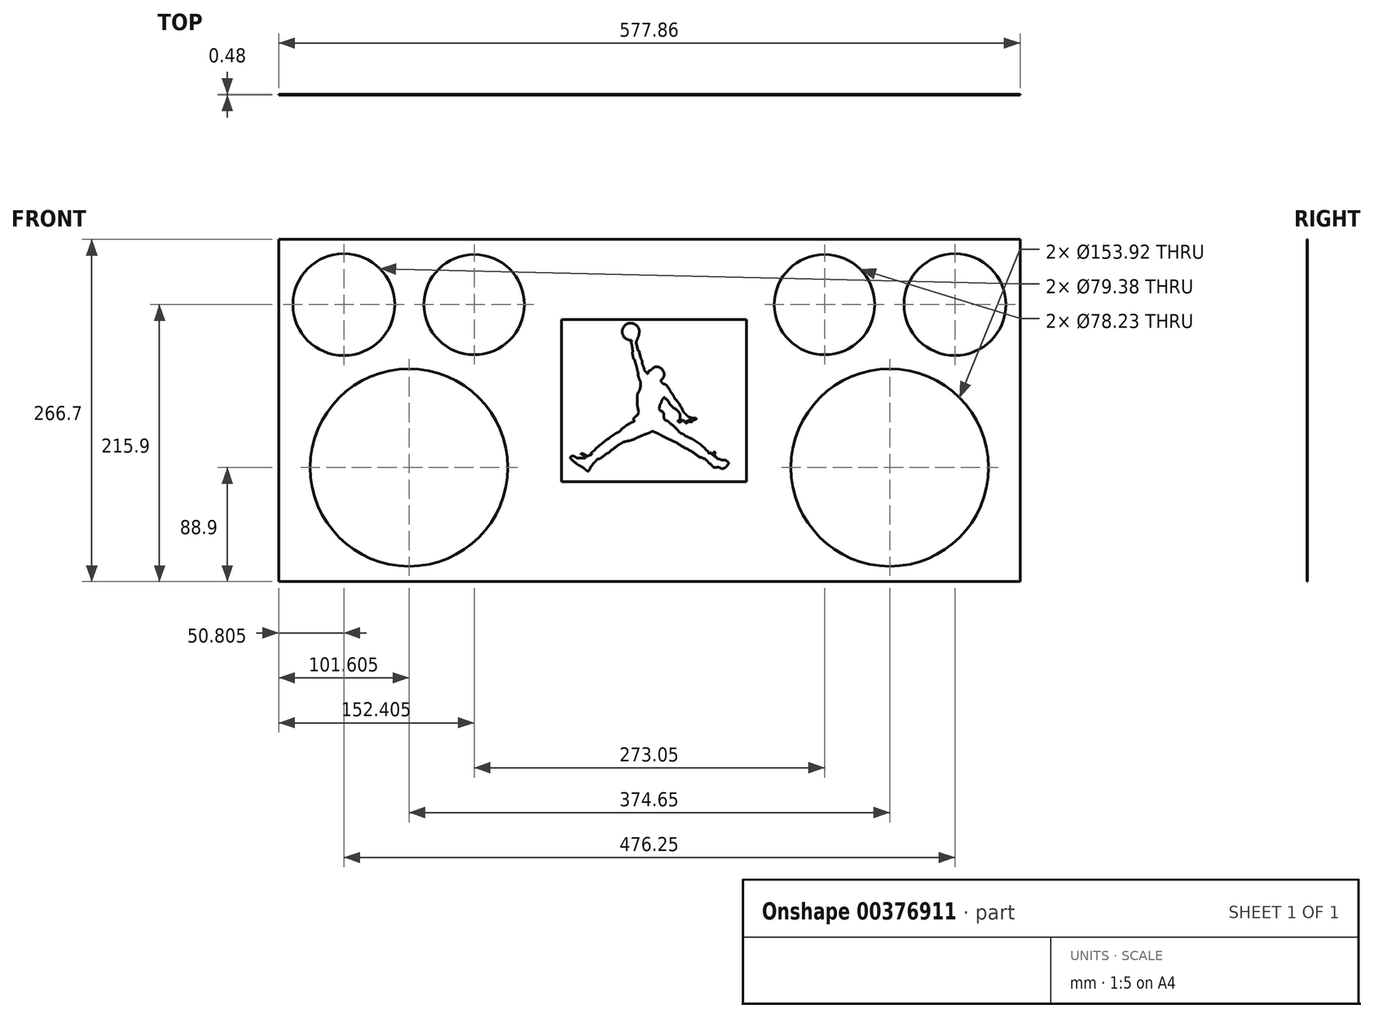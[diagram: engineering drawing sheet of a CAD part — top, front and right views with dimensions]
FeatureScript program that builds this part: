
annotation { "Feature Type Name" : "Feature", "Feature Type Description" : "" }
export const myFeature = defineFeature(function(context is Context, id is Id, definition is map)
    precondition{}
    {
        {
            var Q0;
            Q0=qCreatedBy(makeId("Front.planeOp"),FACE);
            var sketch = newSketch(context, id + "F0", { "sketchPlane" : qUnion([Q0])});
            skLineSegment(sketch, "E0.bottom", {"start": v(288.93, -133.35) * mm, "end": v(-288.92, -133.35) * mm});
            skLineSegment(sketch, "E0.top", {"start": v(288.92, 133.35) * mm, "end": v(-288.93, 133.35) * mm});
            skLineSegment(sketch, "E0.left", {"start": v(288.93, -133.35) * mm, "end": v(288.93, 133.35) * mm});
            skLineSegment(sketch, "E0.right", {"start": v(-288.92, -133.35) * mm, "end": v(-288.93, 133.35) * mm});
            skPoint(sketch, "E0.middle", {"position": v(0, 0) * mm});
            skLineSegment(sketch, "E1.bottom", {"start": v(288.92, 133.35) * mm, "end": v(85.72, 133.35) * mm, "construction": true});
            skLineSegment(sketch, "E1.top", {"start": v(288.93, -133.35) * mm, "end": v(85.73, -133.35) * mm, "construction": true});
            skLineSegment(sketch, "E1.left", {"start": v(288.93, 133.35) * mm, "end": v(288.93, -133.35) * mm, "construction": true});
            skLineSegment(sketch, "E1.right", {"start": v(85.72, 133.35) * mm, "end": v(85.73, -133.35) * mm, "construction": true});
            skLineSegment(sketch, "E2.bottom", {"start": v(-288.93, 133.35) * mm, "end": v(-85.73, 133.35) * mm, "construction": true});
            skLineSegment(sketch, "E2.top", {"start": v(-288.92, -133.35) * mm, "end": v(-85.72, -133.35) * mm, "construction": true});
            skLineSegment(sketch, "E2.left", {"start": v(-288.93, 133.35) * mm, "end": v(-288.92, -133.35) * mm, "construction": true});
            skLineSegment(sketch, "E2.right", {"start": v(-85.73, 133.35) * mm, "end": v(-85.72, -133.35) * mm, "construction": true});
            skLineSegment(sketch, "E3.bottom", {"start": v(288.92, 133.35) * mm, "end": v(187.32, 133.35) * mm, "construction": true});
            skLineSegment(sketch, "E3.top", {"start": v(288.93, -133.35) * mm, "end": v(187.33, -133.35) * mm, "construction": true});
            skLineSegment(sketch, "E3.left", {"start": v(288.92, 133.35) * mm, "end": v(288.93, -133.35) * mm, "construction": true});
            skLineSegment(sketch, "E3.right", {"start": v(187.32, 133.35) * mm, "end": v(187.33, -133.35) * mm, "construction": true});
            skLineSegment(sketch, "E4.bottom", {"start": v(-288.93, 133.35) * mm, "end": v(-187.33, 133.35) * mm, "construction": true});
            skLineSegment(sketch, "E4.top", {"start": v(-288.92, -133.35) * mm, "end": v(-187.33, -133.35) * mm, "construction": true});
            skLineSegment(sketch, "E4.left", {"start": v(-288.93, 133.35) * mm, "end": v(-288.93, -133.35) * mm, "construction": true});
            skLineSegment(sketch, "E4.right", {"start": v(-187.32, 133.35) * mm, "end": v(-187.32, -133.35) * mm, "construction": true});
            skLineSegment(sketch, "E5.bottom", {"start": v(-280.92, -133.35) * mm, "end": v(281.55, -133.35) * mm, "construction": true});
            skLineSegment(sketch, "E5.top", {"start": v(-280.92, -44.45) * mm, "end": v(281.55, -44.45) * mm, "construction": true});
            skLineSegment(sketch, "E5.left", {"start": v(-280.92, -133.35) * mm, "end": v(-280.92, -44.45) * mm, "construction": true});
            skLineSegment(sketch, "E5.right", {"start": v(281.55, -133.35) * mm, "end": v(281.55, -44.45) * mm, "construction": true});
            skCircle(sketch, "E6", {"center": v(-187.33, -44.45) * mm, "radius": 76.96 * mm});
            skCircle(sketch, "E7", {"center": v(187.33, -44.45) * mm, "radius": 76.96 * mm});
            skLineSegment(sketch, "E8.bottom", {"start": v(-279.46, 133.35) * mm, "end": v(276.06, 133.35) * mm, "construction": true});
            skLineSegment(sketch, "E8.top", {"start": v(-279.46, 82.55) * mm, "end": v(276.06, 82.55) * mm, "construction": true});
            skLineSegment(sketch, "E8.left", {"start": v(-279.46, 133.35) * mm, "end": v(-279.46, 82.55) * mm, "construction": true});
            skLineSegment(sketch, "E8.right", {"start": v(276.06, 133.35) * mm, "end": v(276.06, 82.55) * mm, "construction": true});
            skLineSegment(sketch, "E9.bottom", {"start": v(-288.93, 99.85) * mm, "end": v(-238.12, 99.85) * mm, "construction": true});
            skLineSegment(sketch, "E9.top", {"start": v(-288.93, -125.6) * mm, "end": v(-238.12, -125.6) * mm, "construction": true});
            skLineSegment(sketch, "E9.left", {"start": v(-288.93, 99.85) * mm, "end": v(-288.93, -125.6) * mm, "construction": true});
            skLineSegment(sketch, "E9.right", {"start": v(-238.13, 99.85) * mm, "end": v(-238.13, -125.6) * mm, "construction": true});
            skLineSegment(sketch, "E10.bottom", {"start": v(288.93, 112.58) * mm, "end": v(238.12, 112.58) * mm, "construction": true});
            skLineSegment(sketch, "E10.top", {"start": v(288.93, -125.6) * mm, "end": v(238.12, -125.6) * mm, "construction": true});
            skLineSegment(sketch, "E10.left", {"start": v(288.93, 112.58) * mm, "end": v(288.93, -125.6) * mm, "construction": true});
            skLineSegment(sketch, "E10.right", {"start": v(238.12, 112.58) * mm, "end": v(238.12, -125.6) * mm, "construction": true});
            skCircle(sketch, "E11", {"center": v(-238.12, 82.55) * mm, "radius": 39.69 * mm});
            skCircle(sketch, "E12", {"center": v(238.12, 82.55) * mm, "radius": 39.69 * mm});
            skLineSegment(sketch, "E13.bottom", {"start": v(-85.73, 133.35) * mm, "end": v(-136.53, 133.35) * mm, "construction": true});
            skLineSegment(sketch, "E13.top", {"start": v(-85.73, 57.15) * mm, "end": v(-136.53, 57.15) * mm, "construction": true});
            skLineSegment(sketch, "E13.left", {"start": v(-85.73, 133.35) * mm, "end": v(-85.73, 57.15) * mm, "construction": true});
            skLineSegment(sketch, "E13.right", {"start": v(-136.53, 133.35) * mm, "end": v(-136.53, 57.15) * mm, "construction": true});
            skCircle(sketch, "E14", {"center": v(-136.53, 82.55) * mm, "radius": 39.12 * mm});
            skLineSegment(sketch, "E15.bottom", {"start": v(85.72, 133.35) * mm, "end": v(136.52, 133.35) * mm, "construction": true});
            skLineSegment(sketch, "E15.top", {"start": v(85.72, 47.73) * mm, "end": v(136.52, 47.73) * mm, "construction": true});
            skLineSegment(sketch, "E15.left", {"start": v(85.72, 133.35) * mm, "end": v(85.72, 47.73) * mm, "construction": true});
            skLineSegment(sketch, "E15.right", {"start": v(136.52, 133.35) * mm, "end": v(136.52, 47.73) * mm, "construction": true});
            skCircle(sketch, "E16", {"center": v(136.52, 82.55) * mm, "radius": 39.12 * mm});
            skSolve(sketch);
        }
        {
            assignVariable(context, id + "F1", {"name" : "material", "anyValue" : 0.47});
        }
        {
            var Q0;
            Q0=makeQuery(id+"F0.imprint","IMPRINT",FACE,{"disambiguationData":[TD([[makeQuery(id+"F0.imprint","IMPRINT",EDGE,{"derivedFrom":sQuery(id+"F0.wireOp",EDGE,"E0.bottom")}),-1.0]])]});
            extrude(context, id + "F2", {"entities" : qUnion([Q0]), "depth" : (getVariable(context, 'material')) * mm});
        }
        {
            var Q0;
            Q0=makeQuery(id+"F2.opExtrude","CAP_FACE",FACE,{"disambiguationData":[OSD([sQuery(id+"F0.wireOp",EDGE,"E0.bottom"),sQuery(id+"F0.wireOp",EDGE,"E0.top"),sQuery(id+"F0.wireOp",EDGE,"E0.left"),sQuery(id+"F0.wireOp",EDGE,"E0.right"),sQuery(id+"F0.wireOp",EDGE,"E6"),sQuery(id+"F0.wireOp",EDGE,"E7"),sQuery(id+"F0.wireOp",EDGE,"E11"),sQuery(id+"F0.wireOp",EDGE,"E12"),sQuery(id+"F0.wireOp",EDGE,"E14"),sQuery(id+"F0.wireOp",EDGE,"E16")])],"isStart":false});
            var sketch = newSketch(context, id + "F3", { "sketchPlane" : qUnion([Q0])});
            skArc(sketch, "E17.MirrorCS", {"start": v(46.02, -33.08) * mm, "mid": v(46.45, -33.28) * mm, "end": v(46.78, -33.62) * mm});
            skArc(sketch, "E18.MirrorCS", {"start": v(29.12, -9.84) * mm, "mid": v(28.78, -9.84) * mm, "end": v(28.45, -9.72) * mm});
            skLineSegment(sketch, "E19.MirrorCS", {"start": v(27.65, -9.13) * mm, "end": v(26.45, -7.69) * mm});
            skArc(sketch, "E20.MirrorCS", {"start": v(25.86, -7.66) * mm, "mid": v(25.2, -8.36) * mm, "end": v(24.35, -8.84) * mm});
            skArc(sketch, "E21.MirrorCS", {"start": v(48.94, -34.48) * mm, "mid": v(48.74, -34.18) * mm, "end": v(48.6, -33.86) * mm});
            skArc(sketch, "E22.MirrorCS", {"start": v(22.6, -8.8) * mm, "mid": v(22.38, -8.4) * mm, "end": v(22.47, -7.94) * mm});
            skArc(sketch, "E23.MirrorCS", {"start": v(24.1, -6.5) * mm, "mid": v(24.14, -6.74) * mm, "end": v(24.08, -7) * mm});
            skArc(sketch, "E24.MirrorCS", {"start": v(29.13, -8.1) * mm, "mid": v(29.78, -8.23) * mm, "end": v(30.4, -8.49) * mm});
            skArc(sketch, "E25.MirrorCS", {"start": v(50.79, -35.79) * mm, "mid": v(50.51, -35.77) * mm, "end": v(50.54, -35.5) * mm});
            skArc(sketch, "E26.MirrorCS", {"start": v(28.96, -8.36) * mm, "mid": v(29.24, -8.75) * mm, "end": v(29.47, -9.17) * mm});
            skArc(sketch, "E27.MirrorCS", {"start": v(51.39, -35.73) * mm, "mid": v(51.83, -35.97) * mm, "end": v(52.13, -36.38) * mm});
            skArc(sketch, "E28.MirrorCS", {"start": v(46.02, -33.08) * mm, "mid": v(45.92, -32.9) * mm, "end": v(46.09, -32.78) * mm});
            skArc(sketch, "E29.MirrorCS", {"start": v(29.47, -9.17) * mm, "mid": v(29.47, -9.6) * mm, "end": v(29.12, -9.84) * mm});
            skArc(sketch, "E30.MirrorCS", {"start": v(28.9, -3.43) * mm, "mid": v(29.28, -3.81) * mm, "end": v(29.6, -4.23) * mm});
            skArc(sketch, "E31.MirrorCS", {"start": v(28.45, -9.72) * mm, "mid": v(28.03, -9.45) * mm, "end": v(27.65, -9.13) * mm});
            skArc(sketch, "E32.MirrorCS", {"start": v(48.03, -33.13) * mm, "mid": v(48.4, -33.43) * mm, "end": v(48.6, -33.86) * mm});
            skArc(sketch, "E33.MirrorCS", {"start": v(25.86, -7.66) * mm, "mid": v(26.16, -7.56) * mm, "end": v(26.45, -7.69) * mm});
            skArc(sketch, "E34.MirrorCS", {"start": v(24.35, -8.84) * mm, "mid": v(23.47, -9.05) * mm, "end": v(22.6, -8.8) * mm});
            skArc(sketch, "E35.MirrorCS", {"start": v(31.1, -7.2) * mm, "mid": v(31.1, -7.01) * mm, "end": v(31.28, -6.95) * mm});
            skArc(sketch, "E36.MirrorCS", {"start": v(44.95, -39.03) * mm, "mid": v(44.67, -39) * mm, "end": v(44.42, -38.85) * mm});
            skArc(sketch, "E37.MirrorCS", {"start": v(49.85, -33.95) * mm, "mid": v(49.8, -34.26) * mm, "end": v(49.6, -34.5) * mm});
            skArc(sketch, "E38.MirrorCS", {"start": v(22.47, -7.94) * mm, "mid": v(22.86, -7.7) * mm, "end": v(23.29, -7.56) * mm});
            skArc(sketch, "E39.MirrorCS", {"start": v(50.16, -32.51) * mm, "mid": v(50.36, -32.26) * mm, "end": v(50.66, -32.14) * mm});
            skArc(sketch, "E40.MirrorCS", {"start": v(24.08, -7) * mm, "mid": v(23.74, -7.35) * mm, "end": v(23.29, -7.56) * mm});
            skArc(sketch, "E41.MirrorCS", {"start": v(42.81, -37.45) * mm, "mid": v(42.38, -37.46) * mm, "end": v(41.96, -37.35) * mm});
            skArc(sketch, "E42.MirrorCS", {"start": v(24.1, -6.5) * mm, "mid": v(23.99, -6.09) * mm, "end": v(23.98, -5.67) * mm});
            skArc(sketch, "E43.MirrorCS", {"start": v(33.03, -8.88) * mm, "mid": v(32.43, -8.97) * mm, "end": v(31.82, -8.95) * mm});
            skArc(sketch, "E44.MirrorCS", {"start": v(24.1, -4.98) * mm, "mid": v(24.06, -5.33) * mm, "end": v(23.98, -5.67) * mm});
            skArc(sketch, "E45.MirrorCS", {"start": v(31.82, -8.95) * mm, "mid": v(31.08, -8.8) * mm, "end": v(30.4, -8.49) * mm});
            skArc(sketch, "E46.MirrorCS", {"start": v(50.84, -34.3) * mm, "mid": v(50.85, -33.94) * mm, "end": v(50.95, -33.6) * mm});
            skArc(sketch, "E47.MirrorCS", {"start": v(50.84, -34.3) * mm, "mid": v(50.78, -34.92) * mm, "end": v(50.54, -35.5) * mm});
            skArc(sketch, "E48.MirrorCS", {"start": v(28.96, -8.36) * mm, "mid": v(28.95, -8.17) * mm, "end": v(29.13, -8.1) * mm});
            skArc(sketch, "E49.MirrorCS", {"start": v(50.79, -35.79) * mm, "mid": v(51.08, -35.7) * mm, "end": v(51.39, -35.73) * mm});
            skArc(sketch, "E50.MirrorCS", {"start": v(46.1, -32.2) * mm, "mid": v(46.26, -32.5) * mm, "end": v(46.09, -32.78) * mm});
            skArc(sketch, "E51.MirrorCS", {"start": v(52.13, -36.38) * mm, "mid": v(52.19, -36.75) * mm, "end": v(52.18, -37.13) * mm});
            skArc(sketch, "E52.MirrorCS", {"start": v(52.18, -37.13) * mm, "mid": v(52.87, -37.38) * mm, "end": v(53.5, -37.73) * mm});
            skArc(sketch, "E53.MirrorCS", {"start": v(46.78, -33.62) * mm, "mid": v(47, -33.39) * mm, "end": v(47.25, -33.2) * mm});
            skLineSegment(sketch, "E54.MirrorCS", {"start": v(53.5, -37.73) * mm, "end": v(54.22, -37.73) * mm});
            skArc(sketch, "E55.MirrorCS", {"start": v(47.25, -33.2) * mm, "mid": v(47.63, -33.07) * mm, "end": v(48.03, -33.13) * mm});
            skArc(sketch, "E56.MirrorCS", {"start": v(44.95, -39.03) * mm, "mid": v(45.52, -39.68) * mm, "end": v(45.97, -40.41) * mm});
            skArc(sketch, "E57.MirrorCS", {"start": v(49.6, -34.5) * mm, "mid": v(49.26, -34.62) * mm, "end": v(48.94, -34.48) * mm});
            skArc(sketch, "E58.MirrorCS", {"start": v(43.62, -37.88) * mm, "mid": v(44.11, -38.3) * mm, "end": v(44.42, -38.85) * mm});
            skArc(sketch, "E59.MirrorCS", {"start": v(49.85, -33.95) * mm, "mid": v(49.94, -33.22) * mm, "end": v(50.16, -32.51) * mm});
            skArc(sketch, "E60.MirrorCS", {"start": v(43.62, -37.88) * mm, "mid": v(43.19, -37.73) * mm, "end": v(42.81, -37.45) * mm});
            skArc(sketch, "E61.MirrorCS", {"start": v(33.3, -8.37) * mm, "mid": v(33.29, -8.7) * mm, "end": v(33.03, -8.88) * mm});
            skArc(sketch, "E62.MirrorCS", {"start": v(50.66, -32.14) * mm, "mid": v(50.92, -32.3) * mm, "end": v(51.07, -32.58) * mm});
            skArc(sketch, "E63.MirrorCS", {"start": v(51.07, -32.58) * mm, "mid": v(51.1, -33.1) * mm, "end": v(50.95, -33.6) * mm});
            skArc(sketch, "E64.MirrorCS", {"start": v(46.1, -32.2) * mm, "mid": v(44.69, -31.1) * mm, "end": v(43.47, -29.77) * mm});
            skArc(sketch, "E65.MirrorCS", {"start": v(28.9, -3.43) * mm, "mid": v(27.63, -2.26) * mm, "end": v(26.52, -0.93) * mm});
            skArc(sketch, "E66.MirrorCS", {"start": v(56.51, -38.56) * mm, "mid": v(55.33, -38.25) * mm, "end": v(54.22, -37.73) * mm});
            skArc(sketch, "E67.MirrorCS", {"start": v(47.03, -41.37) * mm, "mid": v(46.4, -41) * mm, "end": v(45.97, -40.41) * mm});
            skArc(sketch, "E68.MirrorCS", {"start": v(32.46, -7.87) * mm, "mid": v(32.92, -8.05) * mm, "end": v(33.3, -8.37) * mm});
            skArc(sketch, "E69.MirrorCS", {"start": v(-45.3, -33.5) * mm, "mid": v(-45.42, -33.08) * mm, "end": v(-45.15, -32.72) * mm});
            skArc(sketch, "E70.MirrorCS", {"start": v(40.28, -36.4) * mm, "mid": v(40.5, -36.36) * mm, "end": v(40.7, -36.45) * mm});
            skArc(sketch, "E71.MirrorCS", {"start": v(40.28, -36.4) * mm, "mid": v(40.1, -36.52) * mm, "end": v(39.9, -36.61) * mm});
            skArc(sketch, "E72.MirrorCS", {"start": v(32.36, -5.64) * mm, "mid": v(30.92, -5.06) * mm, "end": v(29.6, -4.23) * mm});
            skArc(sketch, "E73.MirrorCS", {"start": v(-53.02, -33.51) * mm, "mid": v(-52.77, -33.52) * mm, "end": v(-52.52, -33.54) * mm});
            skArc(sketch, "E74.MirrorCS", {"start": v(-49.94, -34.91) * mm, "mid": v(-49.61, -34.87) * mm, "end": v(-49.28, -34.91) * mm});
            skArc(sketch, "E75.MirrorCS", {"start": v(47.56, -41.43) * mm, "mid": v(47.29, -41.43) * mm, "end": v(47.03, -41.37) * mm});
            skArc(sketch, "E76.MirrorCS", {"start": v(36.15, -7) * mm, "mid": v(33.71, -7.2) * mm, "end": v(31.28, -6.95) * mm});
            skArc(sketch, "E77.MirrorCS", {"start": v(-47.65, -35.5) * mm, "mid": v(-48.17, -35.64) * mm, "end": v(-48.68, -35.49) * mm});
            skArc(sketch, "E78.MirrorCS", {"start": v(32.46, -7.87) * mm, "mid": v(31.75, -7.6) * mm, "end": v(31.1, -7.2) * mm});
            skArc(sketch, "E79.MirrorCS", {"start": v(-46.73, -34.77) * mm, "mid": v(-46.28, -34.67) * mm, "end": v(-45.81, -34.72) * mm});
            skArc(sketch, "E80.MirrorCS", {"start": v(-45.05, -34.01) * mm, "mid": v(-45.18, -33.76) * mm, "end": v(-45.3, -33.5) * mm});
            skArc(sketch, "E81.MirrorCS", {"start": v(41.96, -37.35) * mm, "mid": v(41.3, -36.94) * mm, "end": v(40.7, -36.45) * mm});
            skArc(sketch, "E82.MirrorCS", {"start": v(39.9, -36.61) * mm, "mid": v(39.53, -36.66) * mm, "end": v(39.2, -36.52) * mm});
            skArc(sketch, "E83.MirrorCS", {"start": v(-52.08, -34.44) * mm, "mid": v(-50.7, -35.56) * mm, "end": v(-49.66, -37) * mm});
            skArc(sketch, "E84.MirrorCS", {"start": v(-53.1, -34.07) * mm, "mid": v(-53.26, -33.77) * mm, "end": v(-53.02, -33.51) * mm});
            skArc(sketch, "E85.MirrorCS", {"start": v(48.84, -42.78) * mm, "mid": v(48.46, -42.7) * mm, "end": v(48.3, -42.36) * mm});
            skArc(sketch, "E86.MirrorCS", {"start": v(-52.52, -33.54) * mm, "mid": v(-51.08, -33.94) * mm, "end": v(-49.94, -34.91) * mm});
            skArc(sketch, "E87.MirrorCS", {"start": v(47.56, -41.43) * mm, "mid": v(47.99, -41.84) * mm, "end": v(48.3, -42.36) * mm});
            skArc(sketch, "E88.MirrorCS", {"start": v(36.58, -6.55) * mm, "mid": v(36.45, -6.85) * mm, "end": v(36.15, -7) * mm});
            skArc(sketch, "E89.MirrorCS", {"start": v(-48.68, -35.49) * mm, "mid": v(-49, -35.23) * mm, "end": v(-49.28, -34.91) * mm});
            skArc(sketch, "E90.MirrorCS", {"start": v(51.84, -44.49) * mm, "mid": v(51.48, -44.5) * mm, "end": v(51.13, -44.48) * mm});
            skArc(sketch, "E91.MirrorCS", {"start": v(-46.73, -34.77) * mm, "mid": v(-47.17, -35.17) * mm, "end": v(-47.65, -35.5) * mm});
            skArc(sketch, "E92.MirrorCS", {"start": v(-45.05, -34.01) * mm, "mid": v(-45.33, -34.48) * mm, "end": v(-45.81, -34.72) * mm});
            skArc(sketch, "E93.MirrorCS", {"start": v(-45.15, -32.72) * mm, "mid": v(-44.96, -32.63) * mm, "end": v(-44.78, -32.54) * mm});
            skArc(sketch, "E94.MirrorCS", {"start": v(-42.6, -30.7) * mm, "mid": v(-43.6, -31.7) * mm, "end": v(-44.78, -32.54) * mm});
            skLineSegment(sketch, "E95.MirrorCS", {"start": v(-55.98, -37.2) * mm, "end": v(-49.66, -37) * mm});
            skArc(sketch, "E96.MirrorCS", {"start": v(51.13, -44.48) * mm, "mid": v(50.64, -44.45) * mm, "end": v(50.18, -44.29) * mm});
            skArc(sketch, "E97.MirrorCS", {"start": v(-0.7, 29.52) * mm, "mid": v(-0.77, 29.98) * mm, "end": v(-0.72, 30.44) * mm});
            skArc(sketch, "E98.MirrorCS", {"start": v(-53.1, -34.07) * mm, "mid": v(-52.57, -34.22) * mm, "end": v(-52.08, -34.44) * mm});
            skArc(sketch, "E99.MirrorCS", {"start": v(50.18, -44.29) * mm, "mid": v(49.66, -43.92) * mm, "end": v(49.2, -43.49) * mm});
            skArc(sketch, "E100.MirrorCS", {"start": v(49.2, -43.49) * mm, "mid": v(48.96, -43.17) * mm, "end": v(48.84, -42.78) * mm});
            skArc(sketch, "E101.MirrorCS", {"start": v(36.37, -6.12) * mm, "mid": v(36.54, -6.3) * mm, "end": v(36.58, -6.55) * mm});
            skArc(sketch, "E102.MirrorCS", {"start": v(-57.2, -41.15) * mm, "mid": v(-59.48, -39.24) * mm, "end": v(-61.59, -37.13) * mm});
            skArc(sketch, "E103.MirrorCS", {"start": v(-61.59, -37.13) * mm, "mid": v(-61.64, -36.75) * mm, "end": v(-61.53, -36.38) * mm});
            skArc(sketch, "E104.MirrorCS", {"start": v(-61.53, -36.38) * mm, "mid": v(-61, -35.84) * mm, "end": v(-60.3, -35.56) * mm});
            skArc(sketch, "E105.MirrorCS", {"start": v(-60.3, -35.56) * mm, "mid": v(-59.59, -35.49) * mm, "end": v(-58.9, -35.6) * mm});
            skArc(sketch, "E106.MirrorCS", {"start": v(54.84, -44.54) * mm, "mid": v(55.38, -44.8) * mm, "end": v(55.88, -45.15) * mm});
            skArc(sketch, "E107.MirrorCS", {"start": v(-58.9, -35.6) * mm, "mid": v(-57.91, -36.07) * mm, "end": v(-57.02, -36.69) * mm});
            skArc(sketch, "E108.MirrorCS", {"start": v(51.84, -44.49) * mm, "mid": v(53.34, -44.16) * mm, "end": v(54.84, -44.54) * mm});
            skArc(sketch, "E109.MirrorCS", {"start": v(-55.98, -37.2) * mm, "mid": v(-56.52, -36.99) * mm, "end": v(-57.02, -36.69) * mm});
            skArc(sketch, "E110.MirrorCS", {"start": v(-3.6, 30.73) * mm, "mid": v(-2.3, 29.72) * mm, "end": v(-1.41, 28.34) * mm});
            skArc(sketch, "E111.MirrorCS", {"start": v(-1.41, 28.34) * mm, "mid": v(-1.18, 29) * mm, "end": v(-0.7, 29.52) * mm});
            skArc(sketch, "E112.MirrorCS", {"start": v(-3.77, 31.13) * mm, "mid": v(-3.68, 30.93) * mm, "end": v(-3.6, 30.73) * mm});
            skArc(sketch, "E113.MirrorCS", {"start": v(-0.72, 30.44) * mm, "mid": v(-0.58, 30.67) * mm, "end": v(-0.36, 30.82) * mm});
            skArc(sketch, "E114.MirrorCS", {"start": v(-0.36, 30.82) * mm, "mid": v(0.25, 31.04) * mm, "end": v(0.89, 31.18) * mm});
            skArc(sketch, "E115.MirrorCS", {"start": v(-45.74, -43.72) * mm, "mid": v(-45.75, -43.96) * mm, "end": v(-45.81, -44.2) * mm});
            skArc(sketch, "E116.MirrorCS", {"start": v(36.37, -6.12) * mm, "mid": v(34.35, -5.97) * mm, "end": v(32.36, -5.64) * mm});
            skArc(sketch, "E117.MirrorCS", {"start": v(0.89, 31.18) * mm, "mid": v(1.18, 31.58) * mm, "end": v(1.62, 31.82) * mm});
            skArc(sketch, "E118.MirrorCS", {"start": v(3.02, 33.22) * mm, "mid": v(2.35, 32.5) * mm, "end": v(1.62, 31.82) * mm});
            skArc(sketch, "E119.MirrorCS", {"start": v(-47.29, -47.05) * mm, "mid": v(-47.74, -47.27) * mm, "end": v(-48.23, -47.2) * mm});
            skArc(sketch, "E120.MirrorCS", {"start": v(-53.5, -43.46) * mm, "mid": v(-55.43, -42.43) * mm, "end": v(-57.2, -41.15) * mm});
            skArc(sketch, "E121.MirrorCS", {"start": v(58.15, -45.04) * mm, "mid": v(57.02, -45.24) * mm, "end": v(55.88, -45.15) * mm});
            skArc(sketch, "E122.MirrorCS", {"start": v(-7.03, 22.7) * mm, "mid": v(-6.87, 22.25) * mm, "end": v(-6.8, 21.77) * mm});
            skArc(sketch, "E123.MirrorCS", {"start": v(-41.37, -38.86) * mm, "mid": v(-40.78, -38.23) * mm, "end": v(-40.09, -37.71) * mm});
            skArc(sketch, "E124.MirrorCS", {"start": v(-41.37, -38.86) * mm, "mid": v(-42.33, -40.06) * mm, "end": v(-43.51, -41.03) * mm});
            skArc(sketch, "E125.MirrorCS", {"start": v(-43.51, -41.03) * mm, "mid": v(-44.48, -42.5) * mm, "end": v(-45.74, -43.72) * mm});
            skArc(sketch, "E126.MirrorCS", {"start": v(-45.81, -44.2) * mm, "mid": v(-46.43, -45.69) * mm, "end": v(-47.29, -47.05) * mm});
            skArc(sketch, "E127.MirrorCS", {"start": v(-13.9, 52.2) * mm, "mid": v(-14.1, 52.93) * mm, "end": v(-13.95, 53.68) * mm});
            skLineSegment(sketch, "E128.MirrorCS", {"start": v(56.51, -38.56) * mm, "end": v(57.48, -38.58) * mm});
            skArc(sketch, "E129.MirrorCS", {"start": v(-48.23, -47.2) * mm, "mid": v(-49.47, -46.42) * mm, "end": v(-50.53, -45.42) * mm});
            skArc(sketch, "E130.MirrorCS", {"start": v(-53.5, -43.46) * mm, "mid": v(-51.92, -44.3) * mm, "end": v(-50.53, -45.42) * mm});
            skArc(sketch, "E131.MirrorCS", {"start": v(59.8, -38.96) * mm, "mid": v(60.74, -39.62) * mm, "end": v(61.53, -40.47) * mm});
            skArc(sketch, "E132.MirrorCS", {"start": v(61.56, -41.53) * mm, "mid": v(60.89, -42.65) * mm, "end": v(60.07, -43.67) * mm});
            skArc(sketch, "E133.MirrorCS", {"start": v(-6.8, 19.62) * mm, "mid": v(-7.05, 18.06) * mm, "end": v(-7.43, 16.53) * mm});
            skArc(sketch, "E134.MirrorCS", {"start": v(-6.8, 21.77) * mm, "mid": v(-6.77, 20.7) * mm, "end": v(-6.8, 19.62) * mm});
            skArc(sketch, "E135.MirrorCS", {"start": v(60.07, -43.67) * mm, "mid": v(59.18, -44.45) * mm, "end": v(58.15, -45.04) * mm});
            skArc(sketch, "E136.MirrorCS", {"start": v(-7.03, 22.7) * mm, "mid": v(-7.7, 24.05) * mm, "end": v(-8.23, 25.46) * mm});
            skArc(sketch, "E137.MirrorCS", {"start": v(-8.23, 25.46) * mm, "mid": v(-8.62, 26.58) * mm, "end": v(-8.83, 27.74) * mm});
            skArc(sketch, "E138.MirrorCS", {"start": v(-13.14, 44.9) * mm, "mid": v(-13.11, 45.25) * mm, "end": v(-12.97, 45.58) * mm});
            skArc(sketch, "E139.MirrorCS", {"start": v(-12.63, 41.42) * mm, "mid": v(-13, 43.14) * mm, "end": v(-13.14, 44.9) * mm});
            skArc(sketch, "E140.MirrorCS", {"start": v(-13.9, 52.2) * mm, "mid": v(-13.54, 50.63) * mm, "end": v(-13.33, 49.03) * mm});
            skArc(sketch, "E141.MirrorCS", {"start": v(-14.27, 54.74) * mm, "mid": v(-13.78, 54.3) * mm, "end": v(-13.95, 53.68) * mm});
            skLineSegment(sketch, "E142.MirrorCS", {"start": v(-12.97, 45.58) * mm, "end": v(-13.33, 49.03) * mm});
            skArc(sketch, "E143.MirrorCS", {"start": v(11.24, -2.85) * mm, "mid": v(11.32, -3.79) * mm, "end": v(11.28, -4.73) * mm});
            skArc(sketch, "E144.MirrorCS", {"start": v(11.93, -7.09) * mm, "mid": v(11.4, -5.96) * mm, "end": v(11.28, -4.73) * mm});
            skArc(sketch, "E145.MirrorCS", {"start": v(11.43, 26.98) * mm, "mid": v(10.46, 25.05) * mm, "end": v(8.86, 23.6) * mm});
            skArc(sketch, "E146.MirrorCS", {"start": v(-9.89, 54.86) * mm, "mid": v(-10.06, 53.77) * mm, "end": v(-10.4, 52.72) * mm});
            skLineSegment(sketch, "E147.MirrorCS", {"start": v(-10.4, 52.72) * mm, "end": v(-8.93, 46.8) * mm});
            skArc(sketch, "E148.MirrorCS", {"start": v(13.18, -7.85) * mm, "mid": v(12.5, -7.57) * mm, "end": v(11.93, -7.09) * mm});
            skArc(sketch, "E149.MirrorCS", {"start": v(8.86, 23.6) * mm, "mid": v(9.19, 22.98) * mm, "end": v(9.39, 22.3) * mm});
            skArc(sketch, "E150.MirrorCS", {"start": v(-8.93, 46.8) * mm, "mid": v(-8.52, 46.65) * mm, "end": v(-8.29, 46.28) * mm});
            skArc(sketch, "E151.MirrorCS", {"start": v(13.18, -7.85) * mm, "mid": v(14.56, -8.37) * mm, "end": v(15.52, -9.5) * mm});
            skArc(sketch, "E152.MirrorCS", {"start": v(11.17, 20.56) * mm, "mid": v(10.14, 21.3) * mm, "end": v(9.39, 22.3) * mm});
            skArc(sketch, "E153.MirrorCS", {"start": v(11.17, 20.56) * mm, "mid": v(12.03, 20.45) * mm, "end": v(12.82, 20.07) * mm});
            skLineSegment(sketch, "E154.MirrorCS", {"start": v(-8.29, 46.28) * mm, "end": v(-6.93, 41.8) * mm});
            skArc(sketch, "E155.MirrorCS", {"start": v(12.82, 20.07) * mm, "mid": v(13.56, 19.38) * mm, "end": v(14.17, 18.58) * mm});
            skArc(sketch, "E156.MirrorCS", {"start": v(-6.93, 41.8) * mm, "mid": v(-6.95, 41.59) * mm, "end": v(-7.07, 41.42) * mm});
            skArc(sketch, "E157.MirrorCS", {"start": v(-8.83, 27.74) * mm, "mid": v(-8.88, 28.85) * mm, "end": v(-8.86, 29.95) * mm});
            skArc(sketch, "E158.MirrorCS", {"start": v(-5.84, 39.12) * mm, "mid": v(-5.67, 37.95) * mm, "end": v(-5.73, 36.77) * mm});
            skArc(sketch, "E159.MirrorCS", {"start": v(11.04, 9.93) * mm, "mid": v(11.52, 10.08) * mm, "end": v(12.02, 10.08) * mm});
            skArc(sketch, "E160.MirrorCS", {"start": v(-5.73, 36.77) * mm, "mid": v(-4.58, 34) * mm, "end": v(-3.77, 31.13) * mm});
            skArc(sketch, "E161.MirrorCS", {"start": v(-11.46, 39.42) * mm, "mid": v(-12.26, 40.3) * mm, "end": v(-12.63, 41.42) * mm});
            skArc(sketch, "E162.MirrorCS", {"start": v(-11.64, -8.36) * mm, "mid": v(-11.9, -7.95) * mm, "end": v(-12.14, -7.53) * mm});
            skArc(sketch, "E163.MirrorCS", {"start": v(-12.14, -7.53) * mm, "mid": v(-12.2, -6.6) * mm, "end": v(-11.86, -5.75) * mm});
            skArc(sketch, "E164.MirrorCS", {"start": v(8.24, 4.77) * mm, "mid": v(7.95, 2.97) * mm, "end": v(7.48, 1.2) * mm});
            skArc(sketch, "E165.MirrorCS", {"start": v(-11.86, -5.75) * mm, "mid": v(-10.66, -4.6) * mm, "end": v(-9.23, -3.72) * mm});
            skArc(sketch, "E166.MirrorCS", {"start": v(7.48, 1.2) * mm, "mid": v(8.18, 0.43) * mm, "end": v(8.76, -0.43) * mm});
            skArc(sketch, "E167.MirrorCS", {"start": v(8.76, -0.43) * mm, "mid": v(9.66, -0.5) * mm, "end": v(10.41, -1) * mm});
            skArc(sketch, "E168.MirrorCS", {"start": v(-38.33, -37.42) * mm, "mid": v(-39.2, -37.68) * mm, "end": v(-40.09, -37.71) * mm});
            skArc(sketch, "E169.MirrorCS", {"start": v(10.41, -1) * mm, "mid": v(10.94, -1.87) * mm, "end": v(11.24, -2.85) * mm});
            skArc(sketch, "E170.MirrorCS", {"start": v(57.48, -38.58) * mm, "mid": v(58.66, -38.66) * mm, "end": v(59.8, -38.96) * mm});
            skArc(sketch, "E171.MirrorCS", {"start": v(11.25, 29.8) * mm, "mid": v(11.53, 28.4) * mm, "end": v(11.43, 26.98) * mm});
            skArc(sketch, "E172.MirrorCS", {"start": v(-7.43, 16.53) * mm, "mid": v(-7.86, 15.38) * mm, "end": v(-8.46, 14.3) * mm});
            skArc(sketch, "E173.MirrorCS", {"start": v(-7.07, 41.42) * mm, "mid": v(-6.4, 40.3) * mm, "end": v(-5.84, 39.12) * mm});
            skArc(sketch, "E174.MirrorCS", {"start": v(14, 8.46) * mm, "mid": v(12.7, 8.9) * mm, "end": v(12.02, 10.08) * mm});
            skArc(sketch, "E175.MirrorCS", {"start": v(-8.86, 29.95) * mm, "mid": v(-9.45, 31.67) * mm, "end": v(-9.57, 33.49) * mm});
            skArc(sketch, "E176.MirrorCS", {"start": v(-26.54, -18.05) * mm, "mid": v(-25.32, -17.43) * mm, "end": v(-23.98, -17.13) * mm});
            skArc(sketch, "E177.MirrorCS", {"start": v(17.03, 13.8) * mm, "mid": v(18.55, 11.87) * mm, "end": v(19.54, 9.62) * mm});
            skArc(sketch, "E178.MirrorCS", {"start": v(-9.57, 33.49) * mm, "mid": v(-10.7, 36.4) * mm, "end": v(-11.46, 39.42) * mm});
            skArc(sketch, "E179.MirrorCS", {"start": v(11.04, 9.93) * mm, "mid": v(10.2, 8.5) * mm, "end": v(9.18, 7.16) * mm});
            skArc(sketch, "E180.MirrorCS", {"start": v(9.18, 7.16) * mm, "mid": v(9.11, 5.81) * mm, "end": v(8.24, 4.77) * mm});
            skArc(sketch, "E181.MirrorCS", {"start": v(1.86, -16.38) * mm, "mid": v(2.57, -16.27) * mm, "end": v(3.25, -16.47) * mm});
            skArc(sketch, "E182.MirrorCS", {"start": v(1.86, -16.38) * mm, "mid": v(-1, -17.76) * mm, "end": v(-4.03, -18.78) * mm});
            skArc(sketch, "E183.MirrorCS", {"start": v(-9.23, -3.72) * mm, "mid": v(-8.83, -2.5) * mm, "end": v(-8.28, -1.33) * mm});
            skArc(sketch, "E184.MirrorCS", {"start": v(3.02, 33.22) * mm, "mid": v(4.87, 34) * mm, "end": v(6.87, 33.94) * mm});
            skArc(sketch, "E185.MirrorCS", {"start": v(6.87, 33.94) * mm, "mid": v(9.53, 32.36) * mm, "end": v(11.25, 29.8) * mm});
            skArc(sketch, "E186.MirrorCS", {"start": v(-9.56, 7.5) * mm, "mid": v(-9.51, 9.77) * mm, "end": v(-9.34, 12.03) * mm});
            skArc(sketch, "E187.MirrorCS", {"start": v(-8.13, 59.42) * mm, "mid": v(-8.73, 57.03) * mm, "end": v(-9.89, 54.86) * mm});
            skArc(sketch, "E188.MirrorCS", {"start": v(-9.34, 12.03) * mm, "mid": v(-9.04, 13.22) * mm, "end": v(-8.46, 14.3) * mm});
            skArc(sketch, "E189.MirrorCS", {"start": v(61.53, -40.47) * mm, "mid": v(61.64, -41) * mm, "end": v(61.56, -41.53) * mm});
            skArc(sketch, "E190.MirrorCS", {"start": v(21.18, 0.66) * mm, "mid": v(23.3, -1.82) * mm, "end": v(24.1, -4.98) * mm});
            skArc(sketch, "E191.MirrorCS", {"start": v(14.17, 18.58) * mm, "mid": v(15.73, 16.27) * mm, "end": v(17.03, 13.8) * mm});
            skArc(sketch, "E192.MirrorCS", {"start": v(19.54, 9.62) * mm, "mid": v(23.54, 4.69) * mm, "end": v(26.52, -0.93) * mm});
            skArc(sketch, "E193.MirrorCS", {"start": v(32.11, -31.41) * mm, "mid": v(35.78, -33.8) * mm, "end": v(39.2, -36.52) * mm});
            skArc(sketch, "E194.MirrorCS", {"start": v(32.11, -31.41) * mm, "mid": v(26.05, -28.18) * mm, "end": v(20.22, -24.54) * mm});
            skArc(sketch, "E195.MirrorCS", {"start": v(20.22, -24.54) * mm, "mid": v(14.82, -22.28) * mm, "end": v(9.63, -19.57) * mm});
            skArc(sketch, "E196.MirrorCS", {"start": v(3.25, -16.47) * mm, "mid": v(6.5, -17.88) * mm, "end": v(9.63, -19.57) * mm});
            skArc(sketch, "E197.MirrorCS", {"start": v(-4.03, -18.78) * mm, "mid": v(-6.2, -19.79) * mm, "end": v(-8.41, -20.68) * mm});
            skArc(sketch, "E198.MirrorCS", {"start": v(-8.28, -1.33) * mm, "mid": v(-9.2, 3.05) * mm, "end": v(-9.56, 7.5) * mm});
            skArc(sketch, "E199.MirrorCS", {"start": v(-10.28, -21.58) * mm, "mid": v(-9.37, -21.08) * mm, "end": v(-8.41, -20.68) * mm});
            skArc(sketch, "E200.MirrorCS", {"start": v(-10.28, -21.58) * mm, "mid": v(-13.42, -22.94) * mm, "end": v(-16.74, -23.75) * mm});
            skArc(sketch, "E201.MirrorCS", {"start": v(-20.6, -24.73) * mm, "mid": v(-18.68, -24.19) * mm, "end": v(-16.74, -23.75) * mm});
            skArc(sketch, "E202.MirrorCS", {"start": v(-20.6, -24.73) * mm, "mid": v(-21.76, -25.55) * mm, "end": v(-23.04, -26.2) * mm});
            skArc(sketch, "E203.MirrorCS", {"start": v(-25.54, -27.98) * mm, "mid": v(-24.33, -27.03) * mm, "end": v(-23.04, -26.2) * mm});
            skArc(sketch, "E204.MirrorCS", {"start": v(15.52, -9.5) * mm, "mid": v(20.17, -13.23) * mm, "end": v(23.97, -17.83) * mm});
            skArc(sketch, "E205.MirrorCS", {"start": v(-31.4, -32.75) * mm, "mid": v(-28.56, -30.26) * mm, "end": v(-25.54, -27.98) * mm});
            skArc(sketch, "E206.MirrorCS", {"start": v(23.97, -17.83) * mm, "mid": v(26.32, -18.4) * mm, "end": v(28.17, -19.96) * mm});
            skArc(sketch, "E207.MirrorCS", {"start": v(-31.4, -32.75) * mm, "mid": v(-32.38, -33.28) * mm, "end": v(-33.45, -33.56) * mm});
            skArc(sketch, "E208.MirrorCS", {"start": v(-33.45, -33.56) * mm, "mid": v(-35.82, -35.57) * mm, "end": v(-38.33, -37.42) * mm});
            skArc(sketch, "E209.MirrorCS", {"start": v(21.18, 0.66) * mm, "mid": v(16.9, 3.93) * mm, "end": v(14, 8.46) * mm});
            skArc(sketch, "E210.MirrorCS", {"start": v(-42.6, -30.7) * mm, "mid": v(-34.84, -24.02) * mm, "end": v(-26.54, -18.05) * mm});
            skArc(sketch, "E211.MirrorCS", {"start": v(-23.98, -17.13) * mm, "mid": v(-18.36, -11.97) * mm, "end": v(-11.64, -8.36) * mm});
            skArc(sketch, "E212.MirrorCS", {"start": v(-14.27, 54.74) * mm, "mid": v(-18.56, 66.72) * mm, "end": v(-8.13, 59.42) * mm});
            skArc(sketch, "E213.MirrorCS", {"start": v(28.17, -19.96) * mm, "mid": v(36.36, -24.02) * mm, "end": v(43.47, -29.77) * mm});
            skLineSegment(sketch, "E214.bottom", {"start": v(-68.35, 70.75) * mm, "end": v(75.55, 70.75) * mm});
            skLineSegment(sketch, "E214.top", {"start": v(-68.35, -55.47) * mm, "end": v(75.55, -55.47) * mm});
            skLineSegment(sketch, "E214.left", {"start": v(-68.35, 70.75) * mm, "end": v(-68.35, -55.47) * mm});
            skLineSegment(sketch, "E214.right", {"start": v(75.55, 70.75) * mm, "end": v(75.55, -55.47) * mm});
            skSolve(sketch);
        }
        {
            var Q0;
            Q0=makeQuery(id+"F3.imprint","IMPRINT",FACE,{"disambiguationData":[TD([[makeQuery(id+"F3.imprint","IMPRINT",EDGE,{"derivedFrom":sQuery(id+"F3.wireOp",EDGE,"E17.MirrorCS")}),-1.0]])]});
            extrude(context, id + "F4", {"entities" : qUnion([Q0]), "operationType" : NewBodyOperationType.REMOVE, "oppositeDirection" : true, "depth" : (getVariable(context, 'material') / 2) * mm});
        }
    });
